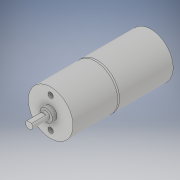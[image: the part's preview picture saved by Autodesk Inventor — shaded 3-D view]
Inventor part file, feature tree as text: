
AUTODESK INVENTOR PART (.ipt)
format: ipt  version: 2017 (Build 210142000, 142)  size: 142,848 bytes
history: native  units: mm
features: extrude x6, sketch x6, other x1, fillet x1, pattern_circular x1
ambient origin geometry x8: Origin, YZ Plane, XZ Plane, XY Plane, X Axis, Y Axis, Z Axis, Center Point
bodies: Body1 (feature_tree)
feature tree (15):
  other  "Твердое тело1"
  extrude  "Выдавливание1"  Depth=25.0mm
  fillet  "Сопряжение1"  Radius=31.0mm
  extrude  "Выдавливание2"  Depth=1.0mm
  extrude  "Выдавливание3"  Depth=25.0mm
  extrude  "Выдавливание4"  Depth=25.0mm TaperAngle=0.0deg
  extrude  "Выдавливание5"  Depth=7.0mm
  extrude  "Выдавливание6"  Depth=2.5mm TaperAngle=0.0deg
  pattern_circular  "Круговой массив1"  [2 undecoded]
  sketch  "Эскиз1"
  sketch  "Эскиз2"
  sketch  "Эскиз3"
  sketch  "Эскиз4"
  sketch  "Эскиз5"
  sketch  "Эскиз6"
note: 2 required parameter values undecoded (feature->parameter linkage not recoverable at this tier; creation-order binding heuristic only, values carry confidence <= 0.55)
